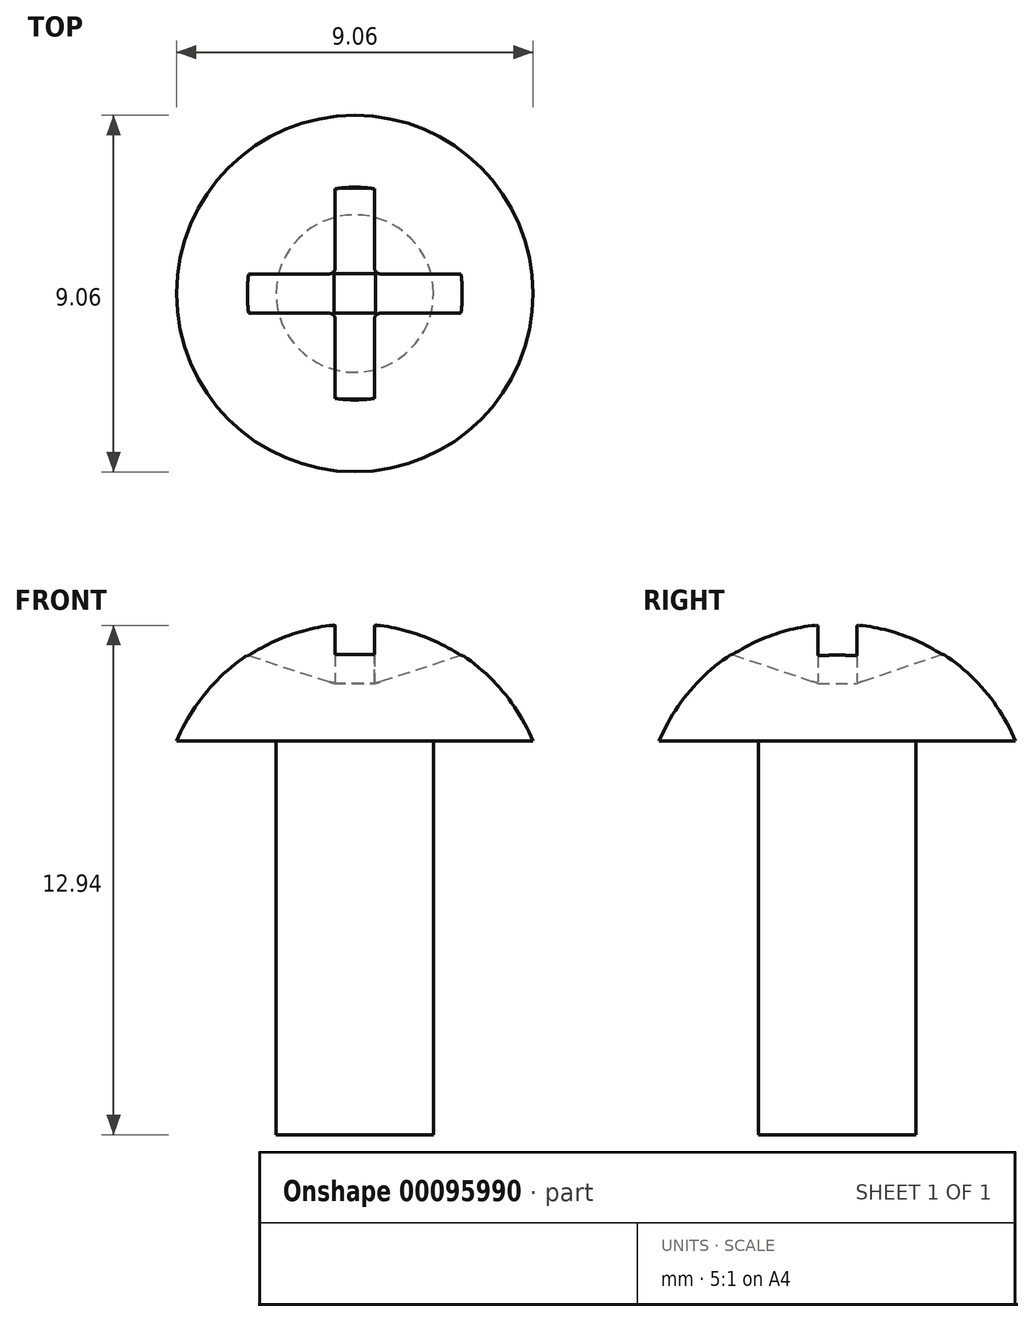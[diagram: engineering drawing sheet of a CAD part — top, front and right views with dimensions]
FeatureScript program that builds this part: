
annotation { "Feature Type Name" : "Feature", "Feature Type Description" : "" }
export const myFeature = defineFeature(function(context is Context, id is Id, definition is map)
    precondition{}
    {
        {
            var Q0;
            Q0=qCreatedBy(makeId("Front.planeOp"),FACE);
            var sketch = newSketch(context, id + "F0", { "sketchPlane" : qUnion([Q0])});
            skArc(sketch, "E0", {"start": v(0, 3) * mm, "mid": v(-2.72, 2.19) * mm, "end": v(-4.53, 0) * mm});
            skLineSegment(sketch, "E1", {"start": v(-4.53, 0) * mm, "end": v(0, 0) * mm});
            skLineSegment(sketch, "E2", {"start": v(0, 0) * mm, "end": v(0, 3) * mm});
            skPoint(sketch, "E3.orphan", {"position": v(4.47, 0) * mm});
            skSolve(sketch);
        }
        {
            var Q0;
            Q0=qCreatedBy(makeId("Front.planeOp"),FACE);
            var sketch = newSketch(context, id + "F1", { "sketchPlane" : qUnion([Q0])});
            skLineSegment(sketch, "E4", {"start": v(0, 7.5) * mm, "end": v(0, -4.4) * mm});
            skSolve(sketch);
        }
        {
            var Q0;
            Q0=makeQuery(id+"F0.imprint","IMPRINT",FACE,{"disambiguationData":[TD([[makeQuery(id+"F0.imprint","IMPRINT",EDGE,{"derivedFrom":sQuery(id+"F0.wireOp",EDGE,"E0")}),1.0]])]});
            var Q1;
            Q1=sQuery(id+"F0.wireOp",EDGE,"E0");
            var Q2;
            Q2=sQuery(id+"F1.wireOp",EDGE,"E4");
            var Q3;
            Q3=sQuery(id+"F1.wireOp",EDGE,"E4");
            revolve(context, id + "F2", {"entities" : qUnion([Q0]), "surfaceEntities" : qUnion([Q1, Q2]), "axis" : qUnion([Q3]), "revolveType" : RevolveType.ONE_DIRECTION, "angle" : 360 * degree});
        }
        {
            var Q0;
            Q0=makeQuery(id+"F2.opRevolve","SWEPT_FACE",FACE,{"disambiguationData":[OSD([sQuery(id+"F0.wireOp",EDGE,"E1")])]});
            var sketch = newSketch(context, id + "F3", { "sketchPlane" : qUnion([Q0])});
            skCircle(sketch, "E5", {"center": v(0, 0) * mm, "radius": 2 * mm});
            skSolve(sketch);
        }
        {
            var Q0;
            Q0 = qSketchRegion(id + "F3", true);
            extrude(context, id + "F4", {"entities" : qUnion([Q0]), "operationType" : NewBodyOperationType.ADD, "depth" : 10 * mm});
        }
        {
            var Q0;
            Q0=qCreatedBy(makeId("Front.planeOp"),FACE);
            var sketch = newSketch(context, id + "F5", { "sketchPlane" : qUnion([Q0])});
            skLineSegment(sketch, "E6.bottom", {"start": v(-0.5, 3) * mm, "end": v(0.5, 3) * mm});
            skLineSegment(sketch, "E6.top", {"start": v(-0.5, 2.2) * mm, "end": v(0.5, 2.2) * mm});
            skLineSegment(sketch, "E6.left", {"start": v(-0.5, 3) * mm, "end": v(-0.5, 2.2) * mm});
            skLineSegment(sketch, "E6.right", {"start": v(0.5, 3) * mm, "end": v(0.5, 2.2) * mm});
            skSolve(sketch);
        }
        {
            var Q0;
            Q0 = qSketchRegion(id + "F5", true);
            extrude(context, id + "F6", {"entities" : qUnion([Q0]), "operationType" : NewBodyOperationType.REMOVE, "oppositeDirection" : true, "depth" : 3 * mm, "hasSecondDirection" : true, "secondDirectionOppositeDirection" : false, "secondDirectionDepth" : 3 * mm});
        }
        {
            var Q0;
            Q0=qCreatedBy(makeId("Right.planeOp"),FACE);
            var sketch = newSketch(context, id + "F7", { "sketchPlane" : qUnion([Q0])});
            skLineSegment(sketch, "E7.bottom", {"start": v(-0.5, 2.98) * mm, "end": v(0.5, 2.98) * mm});
            skLineSegment(sketch, "E7.top", {"start": v(-0.5, 2.18) * mm, "end": v(0.5, 2.18) * mm});
            skLineSegment(sketch, "E7.left", {"start": v(-0.5, 2.98) * mm, "end": v(-0.5, 2.18) * mm});
            skLineSegment(sketch, "E7.right", {"start": v(0.5, 2.98) * mm, "end": v(0.5, 2.18) * mm});
            skSolve(sketch);
        }
        {
            var Q0;
            Q0=makeQuery(id+"F7.imprint","IMPRINT",FACE,{"disambiguationData":[TD([[makeQuery(id+"F7.imprint","IMPRINT",EDGE,{"derivedFrom":sQuery(id+"F7.wireOp",EDGE,"E7.bottom")}),-1.0]])]});
            extrude(context, id + "F8", {"entities" : qUnion([Q0]), "operationType" : NewBodyOperationType.REMOVE, "depth" : 3 * mm, "hasSecondDirection" : true, "secondDirectionOppositeDirection" : true, "secondDirectionDepth" : 3 * mm});
        }
        {
            var Q0;
            Q0=qCreatedBy(makeId("Front.planeOp"),FACE);
            var sketch = newSketch(context, id + "F9", { "sketchPlane" : qUnion([Q0])});
            skLineSegment(sketch, "E8", {"start": v(2.74, 2.19) * mm, "end": v(0.53, 1.47) * mm});
            skLineSegment(sketch, "E9", {"start": v(0.53, 1.47) * mm, "end": v(0, 1.47) * mm});
            skLineSegment(sketch, "E10.MirrorCS", {"start": v(-0.53, 1.47) * mm, "end": v(0, 1.47) * mm});
            skLineSegment(sketch, "E11.MirrorCS", {"start": v(-2.74, 2.19) * mm, "end": v(-0.53, 1.47) * mm});
            skLineSegment(sketch, "E12", {"start": v(2.74, 2.19) * mm, "end": v(-2.74, 2.19) * mm});
            skSolve(sketch);
        }
        {
            var Q0;
            Q0 = qSketchRegion(id + "F9", true);
            extrude(context, id + "F10", {"entities" : qUnion([Q0]), "operationType" : NewBodyOperationType.REMOVE, "depth" : .5 * mm, "hasSecondDirection" : true, "secondDirectionOppositeDirection" : true, "secondDirectionDepth" : .5 * mm});
        }
        {
            var Q0;
            Q0=makeQuery(id+"F8.boolean.opBoolean","INTERSECT",EDGE,{"derivedFrom":[makeQuery(id+"F6.boolean.opBoolean","COPY",FACE,{"derivedFrom":makeQuery(id+"F6.opExtrude","SWEPT_FACE",FACE,{"disambiguationData":[OSD([sQuery(id+"F5.wireOp",EDGE,"E6.top")])]})}),makeQuery(id+"F8.opExtrude","SWEPT_FACE",FACE,{"disambiguationData":[OSD([sQuery(id+"F7.wireOp",EDGE,"E7.right")])]})]});
            chamfer(context, id + "F11", {"entities" : qUnion([Q0]), "chamferType" : ChamferType.TWO_OFFSETS, "width1" : .733 * mm, "oppositeDirection" : true, "width2" : 2.18 * mm, "tangentPropagation" : true});
        }
        {
            var Q0;
            {var subQ0=makeQuery(id+"F8.opExtrude","SWEPT_FACE",FACE,{"disambiguationData":[OSD([sQuery(id+"F7.wireOp",EDGE,"E7.left")])]});var subQ1=makeQuery(id+"F6.boolean.opBoolean","COPY",FACE,{"derivedFrom":makeQuery(id+"F6.opExtrude","SWEPT_FACE",FACE,{"disambiguationData":[OSD([sQuery(id+"F5.wireOp",EDGE,"E6.top")])]})});Q0=makeQuery(id+"F11.opChamfer","BLEND_EDGE",EDGE,{"blendedFrom":[makeQuery(id+"F8.boolean.opBoolean","INTERSECT",EDGE,{"derivedFrom":[subQ1,subQ0]}),makeQuery(id+"F8.boolean.opBoolean","SPLIT",FACE,{"disambiguationData":[TD([subQ0])],"derivedFrom":subQ1})],"blendedInto":[makeQuery(id+"F8.boolean.opBoolean","SPLIT",FACE,{"disambiguationData":[TD([subQ0])],"derivedFrom":subQ1})]});}
            var Q1;
            Q1=makeQuery(id+"F8.boolean.opBoolean","INTERSECT",EDGE,{"derivedFrom":[makeQuery(id+"F6.boolean.opBoolean","COPY",FACE,{"derivedFrom":makeQuery(id+"F6.opExtrude","SWEPT_FACE",FACE,{"disambiguationData":[OSD([sQuery(id+"F5.wireOp",EDGE,"E6.top")])]})}),makeQuery(id+"F8.opExtrude","SWEPT_FACE",FACE,{"disambiguationData":[OSD([sQuery(id+"F7.wireOp",EDGE,"E7.left")])]})]});
            chamfer(context, id + "F12", {"entities" : qUnion([Q0, Q1]), "chamferType" : ChamferType.TWO_OFFSETS, "width1" : 2.18 * mm, "oppositeDirection" : true, "width2" : .73 * mm, "tangentPropagation" : true});
        }
        {
            var Q0;
            Q0=makeQuery(id+"F8.boolean.opBoolean","INTERSECT",EDGE,{"derivedFrom":[makeQuery(id+"F6.boolean.opBoolean","COPY",FACE,{"derivedFrom":makeQuery(id+"F6.opExtrude","SWEPT_FACE",FACE,{"disambiguationData":[OSD([sQuery(id+"F5.wireOp",EDGE,"E6.right")])]})}),makeQuery(id+"F8.opExtrude","SWEPT_FACE",FACE,{"disambiguationData":[OSD([sQuery(id+"F7.wireOp",EDGE,"E7.left")])]})]});
            var Q1;
            Q1=makeQuery(id+"F8.boolean.opBoolean","INTERSECT",EDGE,{"derivedFrom":[makeQuery(id+"F6.boolean.opBoolean","COPY",FACE,{"derivedFrom":makeQuery(id+"F6.opExtrude","SWEPT_FACE",FACE,{"disambiguationData":[OSD([sQuery(id+"F5.wireOp",EDGE,"E6.right")])]})}),makeQuery(id+"F8.opExtrude","SWEPT_FACE",FACE,{"disambiguationData":[OSD([sQuery(id+"F7.wireOp",EDGE,"E7.right")])]})]});
            var Q2;
            Q2=makeQuery(id+"F8.boolean.opBoolean","INTERSECT",EDGE,{"derivedFrom":[makeQuery(id+"F6.boolean.opBoolean","COPY",FACE,{"derivedFrom":makeQuery(id+"F6.opExtrude","SWEPT_FACE",FACE,{"disambiguationData":[OSD([sQuery(id+"F5.wireOp",EDGE,"E6.left")])]})}),makeQuery(id+"F8.opExtrude","SWEPT_FACE",FACE,{"disambiguationData":[OSD([sQuery(id+"F7.wireOp",EDGE,"E7.left")])]})]});
            var Q3;
            Q3=makeQuery(id+"F8.boolean.opBoolean","INTERSECT",EDGE,{"derivedFrom":[makeQuery(id+"F6.boolean.opBoolean","COPY",FACE,{"derivedFrom":makeQuery(id+"F6.opExtrude","SWEPT_FACE",FACE,{"disambiguationData":[OSD([sQuery(id+"F5.wireOp",EDGE,"E6.left")])]})}),makeQuery(id+"F8.opExtrude","SWEPT_FACE",FACE,{"disambiguationData":[OSD([sQuery(id+"F7.wireOp",EDGE,"E7.right")])]})]});
            fillet(context, id + "F13", {"entities" : qUnion([Q0, Q1, Q2, Q3]), "radius" : .15 * mm, "tangentPropagation" : true, "allowEdgeOverflow" : false});
        }
    });
